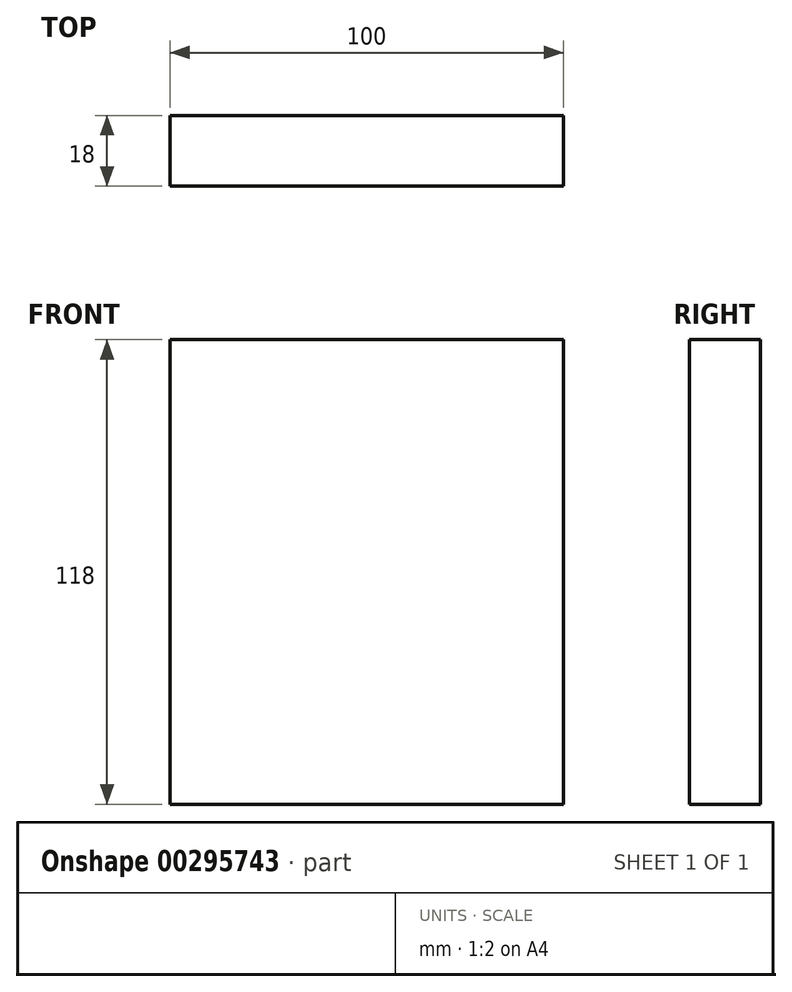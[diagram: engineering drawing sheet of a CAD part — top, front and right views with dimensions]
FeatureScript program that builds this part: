
annotation { "Feature Type Name" : "Feature", "Feature Type Description" : "" }
export const myFeature = defineFeature(function(context is Context, id is Id, definition is map)
    precondition{}
    {
        {
            var Q0;
            Q0=qCreatedBy(makeId("Front.planeOp"),FACE);
            var sketch = newSketch(context, id + "F0", { "sketchPlane" : qUnion([Q0])});
            skLineSegment(sketch, "E0.bottom", {"start": v(-88.46, 107.06) * mm, "end": v(11.54, 107.06) * mm});
            skLineSegment(sketch, "E0.top", {"start": v(-88.46, -10.94) * mm, "end": v(11.54, -10.94) * mm});
            skLineSegment(sketch, "E0.left", {"start": v(-88.46, 107.06) * mm, "end": v(-88.46, -10.94) * mm});
            skLineSegment(sketch, "E0.right", {"start": v(11.54, 107.06) * mm, "end": v(11.54, -10.94) * mm});
            skSolve(sketch);
        }
        {
            var Q0;
            Q0=makeQuery(id+"F0.imprint","IMPRINT",FACE,{"disambiguationData":[TD([[makeQuery(id+"F0.imprint","IMPRINT",EDGE,{"derivedFrom":sQuery(id+"F0.wireOp",EDGE,"E0.bottom")}),-1.0]])]});
            extrude(context, id + "F1", {"entities" : qUnion([Q0]), "depth" : 18 * mm});
        }
    });
